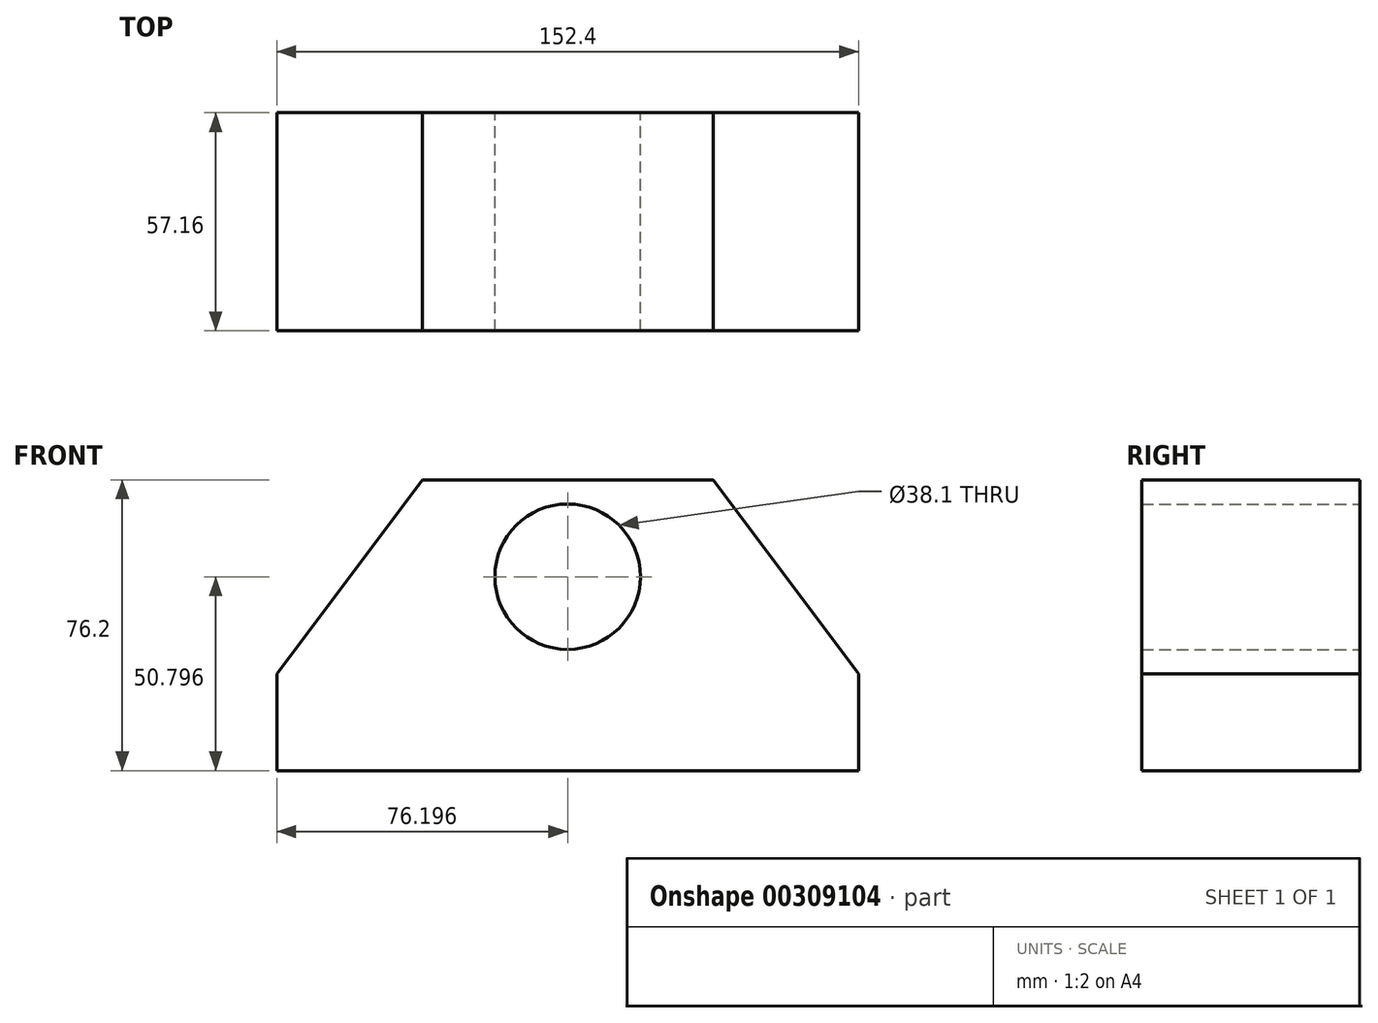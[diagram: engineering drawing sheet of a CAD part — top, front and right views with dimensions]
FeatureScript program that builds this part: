
annotation { "Feature Type Name" : "Feature", "Feature Type Description" : "" }
export const myFeature = defineFeature(function(context is Context, id is Id, definition is map)
    precondition{}
    {
        {
            var Q0;
            Q0=qCreatedBy(makeId("Front.planeOp"),FACE);
            var sketch = newSketch(context, id + "F0", { "sketchPlane" : qUnion([Q0])});
            skLineSegment(sketch, "E0", {"start": v(-61.77, -21.55) * mm, "end": v(90.63, -21.55) * mm});
            skLineSegment(sketch, "E1", {"start": v(90.63, -21.55) * mm, "end": v(90.63, 3.85) * mm});
            skLineSegment(sketch, "E2", {"start": v(-61.77, 3.85) * mm, "end": v(-61.77, -21.55) * mm});
            skLineSegment(sketch, "E3", {"start": v(-61.77, 3.85) * mm, "end": v(-23.67, 54.65) * mm});
            skLineSegment(sketch, "E4", {"start": v(-23.67, 54.65) * mm, "end": v(52.53, 54.65) * mm});
            skLineSegment(sketch, "E5", {"start": v(52.53, 54.65) * mm, "end": v(90.63, 3.85) * mm});
            skCircle(sketch, "E6", {"center": v(14.43, 29.25) * mm, "radius": 19.05 * mm});
            skSolve(sketch);
        }
        {
            var Q0;
            Q0=makeQuery(id+"F0.imprint","IMPRINT",FACE,{"disambiguationData":[TD([[makeQuery(id+"F0.imprint","IMPRINT",EDGE,{"derivedFrom":sQuery(id+"F0.wireOp",EDGE,"E0")}),1.0]])]});
            extrude(context, id + "F1", {"entities" : qUnion([Q0]), "depth" : 57.15 * mm, "symmetric" : true});
        }
    });
